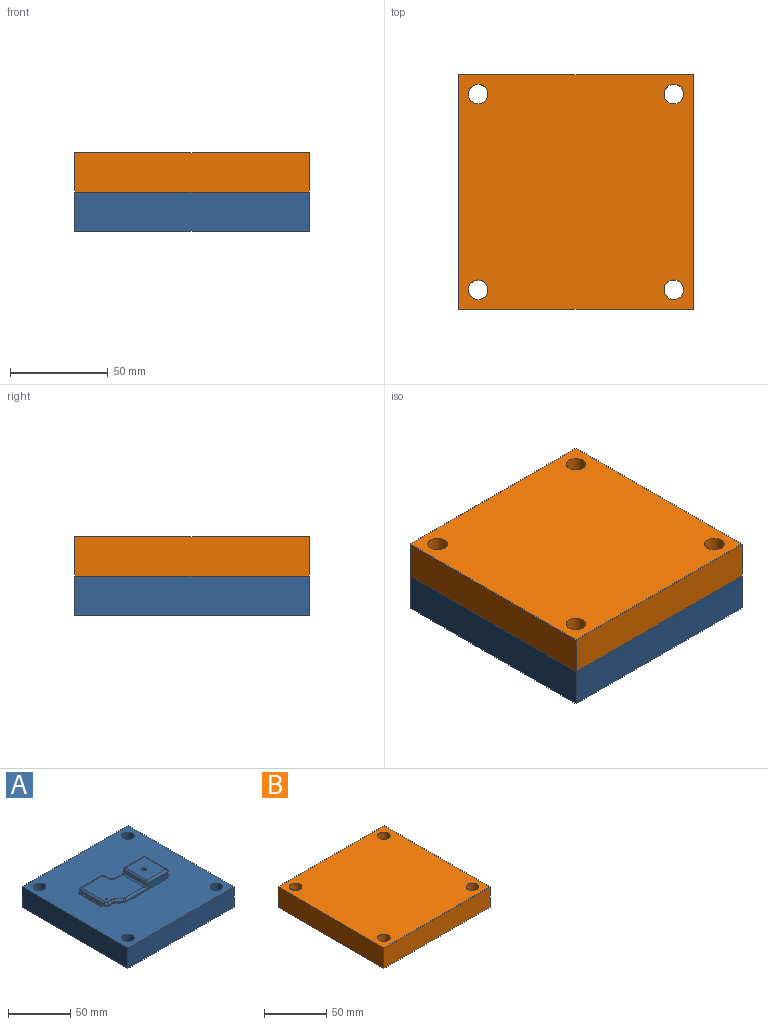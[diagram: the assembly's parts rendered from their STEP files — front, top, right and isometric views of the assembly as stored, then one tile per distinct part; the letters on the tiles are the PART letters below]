
ASSEMBLY  parts=2 mates=1
PART A: 67 faces, bbox 120x120x28 mm
  f0: plane 120x120mm, normal (0,0,1), area 12010.1mm2, adj f1,f2,f3,f4,f6,f7,f8,f9
  f1: plane 120x20mm, normal (0,1,0), area 2400mm2, adj f0,f2,f4,f5
  f2: plane 120x20mm, normal (-1,0,0), area 2400mm2, adj f0,f1,f3,f5
  f3: plane 120x20mm, normal (0,-1,0), area 2400mm2, adj f0,f2,f4,f5
  f4: plane 120x20mm, normal (1,0,0), area 2400mm2, adj f0,f1,f3,f5
  f5: plane 120x120mm, normal (0,0,-1), area 14070.1mm2, adj f1,f2,f3,f4,f6,f7,f8,f9
  f6: cylinder r=5mm len=20mm, axis (0,0,1), area 628.3mm2, adj f0,f5
  f7: cylinder r=5mm len=20mm, axis (0,0,1), area 628.3mm2, adj f0,f5
  f8: cylinder r=5mm len=20mm, axis (0,0,1), area 628.3mm2, adj f0,f5
  f9: cylinder r=5mm len=20mm, axis (0,0,1), area 628.3mm2, adj f0,f5
  f10: plane 22x1mm, normal (0,1,0), area 22mm2, adj f0,f19,f20,f43
  f11: plane 26.05x1mm, normal (-1,0,0), area 26.1mm2, adj f0,f20,f21,f35
  f12: plane 3.91x1mm, normal (0,-1,0), area 3.9mm2, adj f0,f21,f22,f29
  f13: plane 5.42x4.55mm, normal (-0.64,-0.77,0), area 7.1mm2, adj f0,f22,f23,f28
  f14: plane 46.82x6mm, normal (0,-1,0), area 151.8mm2, adj f0,f23,f30,f34,f38,f39
  f15: plane 24x6mm, normal (1,0,0), area 144mm2, adj f0,f30,f36,f37
  f16: plane 32x6mm, normal (0,1,0), area 137mm2, adj f0,f24,f36,f44,f49,f51
  f17: plane 4x1mm, normal (1,0,0), area 4mm2, adj f0,f19,f24,f48
  f18: plane 36x34mm, normal (0,0,1), area 1044.8mm2, adj f27,f28,f29,f31,f32,f34,f35,f40
  f19: cylinder r=3mm len=3mm, axis (0,0,1), area 4.7mm2, adj f0,f10,f17,f46
  f20: cylinder r=3mm len=3mm, axis (0,0,1), area 4.7mm2, adj f0,f10,f11,f40
  f21: cylinder r=3mm len=3mm, axis (0,0,-1), area 4.7mm2, adj f0,f11,f12,f32
  f22: cylinder r=3mm len=1.93mm, axis (0,0,-1), area 2.1mm2, adj f0,f12,f13,f27
  f23: cylinder r=3mm len=1.93mm, axis (0,0,-1), area 2.1mm2, adj f0,f13,f14,f31
  f24: cylinder r=3mm len=3mm, axis (0,0,1), area 4.7mm2, adj f0,f16,f17,f50
  f25: plane 24x1mm, normal (-1,0,0), area 24mm2, adj f39,f45,f49,f53
  f26: plane 24x21mm, normal (0,0,1), area 491.4mm2, adj f37,f38,f44,f45,f65
  f27: torus R=5mm, axis (0,0,1), area 8.2mm2, adj f18,f22,f28,f29
  f28: cylinder r=2mm len=6.7mm, axis (0.77,-0.64,0), area 22.2mm2, adj f13,f18,f27,f31
  f29: cylinder r=2mm len=3.91mm, axis (1,0,0), area 12.3mm2, adj f12,f18,f27,f32
  f30: cylinder r=2mm len=6mm, axis (0,0,-1), area 18.8mm2, adj f0,f14,f15,f33
  f31: torus R=1mm, axis (0,0,1), area 5mm2, adj f18,f23,f28,f34
  f32: torus R=1mm, axis (0,0,1), area 11.2mm2, adj f18,f21,f29,f35
  f33: sphere r=2mm, area 6.3mm2, adj f30,f37,f38
  f34: cylinder r=2mm len=25.82mm, axis (1,0,0), area 73.1mm2, adj f14,f18,f31,f52
  f35: cylinder r=2mm len=26.05mm, axis (0,-1,0), area 81.8mm2, adj f11,f18,f32,f40
  f36: cylinder r=2mm len=6mm, axis (0,0,1), area 18.8mm2, adj f0,f15,f16,f41
  f37: cylinder r=2mm len=24mm, axis (0,1,0), area 75.4mm2, adj f15,f26,f33,f41
  f38: cylinder r=2mm len=21mm, axis (1,0,0), area 66mm2, adj f14,f26,f33,f42
  f39: cylinder r=2mm len=5mm, axis (0,0,-1), area 7.7mm2, adj f14,f25,f42,f52
  f40: torus R=1mm, axis (0,0,1), area 11.2mm2, adj f18,f20,f35,f43
  f41: sphere r=2mm, area 6.3mm2, adj f36,f37,f44
  f42: sphere r=2mm, area 6.3mm2, adj f38,f39,f45
  f43: cylinder r=2mm len=22mm, axis (-1,0,0), area 69.1mm2, adj f10,f18,f40,f46
  f44: cylinder r=2mm len=21mm, axis (-1,0,0), area 66mm2, adj f16,f26,f41,f47
  f45: cylinder r=2mm len=24mm, axis (0,-1,0), area 75.4mm2, adj f25,f26,f42,f47
  f46: torus R=1mm, axis (0,0,1), area 11.2mm2, adj f18,f19,f43,f48
  f47: sphere r=2mm, area 6.3mm2, adj f44,f45,f49
  f48: cylinder r=2mm len=4mm, axis (0,1,0), area 12.6mm2, adj f17,f18,f46,f50
  f49: cylinder r=2mm len=5mm, axis (0,0,1), area 7.7mm2, adj f16,f25,f47,f54
  f50: torus R=5mm, axis (0,0,1), area 18.4mm2, adj f18,f24,f48,f51
  f51: cylinder r=2mm len=11mm, axis (-1,0,0), area 26.6mm2, adj f16,f18,f50,f54
  f52: bspline ~4x4mm, area 7.6mm2, adj f34,f39,f53
  f53: cylinder r=2mm len=24mm, axis (0,1,0), area 75.4mm2, adj f18,f25,f52,f54
  f54: bspline ~4x4mm, area 7.6mm2, adj f49,f51,f53
  f55: plane 26.05x1.5mm, normal (1,0,0), area 39.1mm2, adj f0,f56,f58,f59
  f56: plane 1.5x1mm, normal (0,1,0), area 1.5mm2, adj f0,f55,f57,f59
  f57: plane 26.05x1.5mm, normal (-1,0,0), area 39.1mm2, adj f0,f56,f58,f59
  f58: plane 1.5x1mm, normal (0,-1,0), area 1.5mm2, adj f0,f55,f57,f59
  f59: plane 26.05x1mm, normal (0,0,1), area 26.1mm2, adj f55,f56,f57,f58
  f60: plane 1.5x1mm, normal (0,1,0), area 1.5mm2, adj f0,f61,f63,f64
  f61: plane 24x1.5mm, normal (-1,0,0), area 36mm2, adj f0,f60,f62,f64
  f62: plane 1.5x1mm, normal (0,-1,0), area 1.5mm2, adj f0,f61,f63,f64
  f63: plane 24x1.5mm, normal (1,0,0), area 36mm2, adj f0,f60,f62,f64
  f64: plane 24x1mm, normal (0,0,1), area 24mm2, adj f60,f61,f62,f63
  f65: cylinder r=2mm len=28mm, axis (0,0,1), area 351.9mm2, adj f5,f26
  f66: cylinder r=1mm len=23mm, axis (0,0,1), area 144.5mm2, adj f5,f18
PART B: 57 faces, bbox 120x120x20.1 mm
  f0: plane 49.76x7mm, normal (0,1,0), area 225.2mm2, adj f2,f11,f21,f41,f46,f50,f51
  f1: plane 28x1.1mm, normal (1,0,0), area 27.6mm2, adj f47,f48,f49,f51,f52,f53,f54,f55
  f2: cylinder r=3mm len=7mm, axis (0,0,1), area 33mm2, adj f0,f21,f24,f45
  f3: cylinder r=3mm len=7mm, axis (0,0,-1), area 33mm2, adj f7,f21,f24,f43
  f4: plane 26x2mm, normal (0,-1,0), area 52mm2, adj f8,f9,f21,f33
  f5: plane 30x2mm, normal (1,0,0), area 60mm2, adj f9,f10,f21,f35
  f6: plane 4x2mm, normal (-1,0,0), area 8mm2, adj f8,f21,f26,f31
  f7: plane 31x7mm, normal (0,-1,0), area 187.7mm2, adj f3,f21,f26,f29,f42,f55,f56
  f8: cylinder r=3mm len=3mm, axis (0,0,-1), area 9.4mm2, adj f4,f6,f21,f32
  f9: cylinder r=3mm len=3mm, axis (0,0,-1), area 9.4mm2, adj f4,f5,f21,f34
  f10: cylinder r=3mm len=3mm, axis (0,0,1), area 9.4mm2, adj f5,f21,f22,f36
  f11: cylinder r=3mm len=2mm, axis (0,0,1), area 4.2mm2, adj f0,f21,f23,f40
  f12: plane 120x20mm, normal (0,1,0), area 2400mm2, adj f13,f15,f20,f21
  f13: plane 120x20mm, normal (-1,0,0), area 2400mm2, adj f12,f14,f20,f21
  f14: plane 120x20mm, normal (0,-1,0), area 2400mm2, adj f13,f15,f20,f21
  f15: plane 120x20mm, normal (1,0,0), area 2400mm2, adj f12,f14,f20,f21
  f16: cylinder r=5mm len=20mm, axis (0,0,1), area 628.3mm2, adj f20,f21
  f17: cylinder r=5mm len=20mm, axis (0,0,1), area 628.3mm2, adj f20,f21
  f18: cylinder r=5mm len=20mm, axis (0,0,1), area 628.3mm2, adj f20,f21
  f19: cylinder r=5mm len=20mm, axis (0,0,1), area 628.3mm2, adj f20,f21
  f20: plane 120x120mm, normal (0,0,1), area 14085.8mm2, adj f12,f13,f14,f15,f16,f17,f18,f19
  f21: plane 120x120mm, normal (0,0,-1), area 11635mm2, adj f0,f2,f3,f4,f5,f6,f7,f8
  f22: plane 3.91x2mm, normal (0,1,0), area 7.8mm2, adj f10,f21,f25,f37
  f23: plane 5.48x4.6mm, normal (0.64,0.77,0), area 14.3mm2, adj f11,f21,f25,f39
  f24: plane 26x7mm, normal (-1,0,0), area 182mm2, adj f2,f3,f21,f44
  f25: cylinder r=3mm len=2mm, axis (0,0,1), area 4.2mm2, adj f21,f22,f23,f38
  f26: cylinder r=3mm len=3mm, axis (0,0,-1), area 9.4mm2, adj f6,f7,f21,f30
  f27: plane 36x35mm, normal (0,0,-1), area 1120.3mm2, adj f29,f30,f31,f33,f35,f37,f38,f39
  f28: plane 26x24mm, normal (0,0,-1), area 624mm2, adj f42,f44,f46,f53
  f29: cylinder r=3mm len=3mm, axis (1,0,0), area 14.1mm2, adj f7,f27,f30,f49
  f30: torus R=6mm, axis (0,0,1), area 30.3mm2, adj f26,f27,f29,f31
  f31: cylinder r=3mm len=4mm, axis (0,-1,0), area 18.8mm2, adj f6,f27,f30,f32
  f32: sphere r=3mm, area 14.1mm2, adj f8,f31,f33
  f33: cylinder r=3mm len=26mm, axis (1,0,0), area 122.5mm2, adj f4,f27,f32,f34
  f34: sphere r=3mm, area 14.1mm2, adj f9,f33,f35
  f35: cylinder r=3mm len=30mm, axis (0,1,0), area 141.4mm2, adj f5,f27,f34,f36
  f36: sphere r=3mm, area 14.1mm2, adj f10,f35,f37
  f37: cylinder r=3mm len=3.91mm, axis (-1,0,0), area 18.4mm2, adj f22,f27,f36,f38
  f38: torus R=6mm, axis (0,0,1), area 13.5mm2, adj f25,f27,f37,f39
  f39: cylinder r=3mm len=7.41mm, axis (-0.77,0.64,0), area 33.7mm2, adj f23,f27,f38,f40
  f40: sphere r=3mm, area 6.3mm2, adj f11,f39,f41
  f41: cylinder r=3mm len=21.76mm, axis (-1,0,0), area 102.5mm2, adj f0,f27,f40,f47
  f42: cylinder r=3mm len=24mm, axis (1,0,0), area 113.1mm2, adj f7,f28,f43,f54
  f43: sphere r=3mm, area 14.1mm2, adj f3,f42,f44
  f44: cylinder r=3mm len=26mm, axis (0,-1,0), area 122.5mm2, adj f24,f28,f43,f45
  f45: sphere r=3mm, area 14.1mm2, adj f2,f44,f46
  f46: cylinder r=3mm len=24mm, axis (-1,0,0), area 113.1mm2, adj f0,f28,f45,f52
  f47: torus R=5mm, axis (-1,0,0), area 6.6mm2, adj f1,f41,f48,f50
  f48: cylinder r=2mm len=26mm, axis (0,-1,0), area 81.7mm2, adj f1,f27,f47,f49
  f49: torus R=5mm, axis (-1,0,0), area 6.6mm2, adj f1,f29,f48,f56
  f50: bspline ~5.74x4mm, area 11.2mm2, adj f0,f47,f51
  f51: cylinder r=2mm len=2mm, axis (0,0,1), area 0.3mm2, adj f0,f1,f50,f52
  f52: torus R=1mm, axis (-1,0,0), area 11.2mm2, adj f1,f46,f51,f53
  f53: cylinder r=2mm len=26mm, axis (0,1,0), area 81.7mm2, adj f1,f28,f52,f54
  f54: torus R=1mm, axis (-1,0,0), area 11.2mm2, adj f1,f42,f53,f55
  f55: cylinder r=2mm len=2mm, axis (0,0,-1), area 0.3mm2, adj f1,f7,f54,f56
  f56: bspline ~4.9x4mm, area 11.2mm2, adj f7,f49,f55
PLACE A t=(5.55,6.27,164.5)mm
PLACE B t=(5.55,6.27,184.5)mm
MATE fastened B.f21 <-> A.f0  axis (0,0,-1) through (5.55,66.27,184.5)mm
